annotation { "Feature Type Name" : "Feature", "Feature Type Description" : "" }
export const myFeature = defineFeature(function(context is Context, id is Id, definition is map)
    precondition{}
    {
        {
            var Q0;
            Q0=qCreatedBy(makeId("Top.planeOp"),FACE);
            var sketch = newSketch(context, id + "F0", { "sketchPlane" : qUnion([Q0])});
            skLineSegment(sketch, "E0.bottom", {"start": v(30.53, 26.5) * mm, "end": v(-34.5, 26.5) * mm});
            skLineSegment(sketch, "E0.top", {"start": v(32.26, -26.5) * mm, "end": v(-34.5, -26.5) * mm});
            skLineSegment(sketch, "E0.left", {"start": v(34.5, 10.5) * mm, "end": v(34.5, -21.5) * mm});
            skLineSegment(sketch, "E0.right", {"start": v(-34.5, 26.5) * mm, "end": v(-34.5, -26.5) * mm});
            skPoint(sketch, "E0.middle", {"position": v(0, 0) * mm});
            skPoint(sketch, "E1", {"position": v(32.26, -26.5) * mm});
            skLineSegment(sketch, "E2", {"start": v(32.26, -26.5) * mm, "end": v(32.26, -23.5) * mm});
            skLineSegment(sketch, "E3", {"start": v(32.26, -23.5) * mm, "end": v(34.5, -21.5) * mm});
            skLineSegment(sketch, "E4", {"start": v(32.26, 25.5) * mm, "end": v(32.26, 12.5) * mm});
            skLineSegment(sketch, "E5", {"start": v(32.26, 12.5) * mm, "end": v(34.5, 10.5) * mm});
            skPoint(sketch, "E6.orphan", {"position": v(34.5, 26.5) * mm});
            skPoint(sketch, "E7.orphan", {"position": v(34.5, -26.5) * mm});
            skLineSegment(sketch, "E8", {"start": v(30.53, 26.5) * mm, "end": v(32.26, 25.5) * mm});
            skPoint(sketch, "E9", {"position": v(32.26, 25.5) * mm});
            skPoint(sketch, "E10", {"position": v(32.26, 26.5) * mm});
            skLineSegment(sketch, "E11", {"start": v(32.26, 25.5) * mm, "end": v(30.53, 26.5) * mm});
            skLineSegment(sketch, "E12.bottom", {"start": v(31.26, 25.5) * mm, "end": v(11.26, 25.5) * mm});
            skLineSegment(sketch, "E12.top", {"start": v(31.26, 23.5) * mm, "end": v(11.26, 23.5) * mm});
            skLineSegment(sketch, "E12.left", {"start": v(32.26, 25.5) * mm, "end": v(32.26, 23.5) * mm});
            skLineSegment(sketch, "E12.right", {"start": v(11.26, 25.5) * mm, "end": v(11.26, 23.5) * mm});
            skLineSegment(sketch, "E13", {"start": v(31.26, 25.5) * mm, "end": v(31.26, 23.5) * mm});
            skLineSegment(sketch, "E14.bottom", {"start": v(10.26, 23.5) * mm, "end": v(-9.74, 23.5) * mm});
            skLineSegment(sketch, "E14.top", {"start": v(10.26, 25.5) * mm, "end": v(-9.74, 25.5) * mm});
            skLineSegment(sketch, "E14.left", {"start": v(11.26, 23.5) * mm, "end": v(11.26, 25.5) * mm});
            skLineSegment(sketch, "E14.right", {"start": v(-9.74, 23.5) * mm, "end": v(-9.74, 25.5) * mm});
            skLineSegment(sketch, "E15", {"start": v(10.26, 25.5) * mm, "end": v(10.26, 23.5) * mm});
            skPoint(sketch, "E16", {"position": v(32.26, -25.5) * mm});
            skLineSegment(sketch, "E17.bottom", {"start": v(31.26, -25.5) * mm, "end": v(16.26, -25.5) * mm});
            skLineSegment(sketch, "E17.top", {"start": v(31.26, -23.5) * mm, "end": v(16.26, -23.5) * mm});
            skLineSegment(sketch, "E17.left", {"start": v(32.26, -25.5) * mm, "end": v(32.26, -23.5) * mm});
            skLineSegment(sketch, "E17.right", {"start": v(0.26, -25.5) * mm, "end": v(0.26, -23.5) * mm});
            skLineSegment(sketch, "E18", {"start": v(31.26, -23.5) * mm, "end": v(31.26, -25.5) * mm});
            skLineSegment(sketch, "E19", {"start": v(16.26, -23.5) * mm, "end": v(16.26, -25.5) * mm});
            skLineSegment(sketch, "E20", {"start": v(15.26, -23.5) * mm, "end": v(15.26, -25.5) * mm});
            skLineSegment(sketch, "E21.trimOffspring", {"start": v(15.26, -23.5) * mm, "end": v(0.26, -23.5) * mm});
            skLineSegment(sketch, "E22.trimOffspring", {"start": v(15.26, -25.5) * mm, "end": v(0.26, -25.5) * mm});
            skCircle(sketch, "E23", {"center": v(32, -19) * mm, "radius": 1.5 * mm});
            skCircle(sketch, "E24", {"center": v(32, 8) * mm, "radius": 1.5 * mm});
            skCircle(sketch, "E25", {"center": v(-19, -24) * mm, "radius": 1.5 * mm});
            skCircle(sketch, "E26", {"center": v(-19, 24) * mm, "radius": 1.5 * mm});
            skLineSegment(sketch, "E27.bottom", {"start": v(-34.5, 6.5) * mm, "end": v(-33.5, 6.5) * mm});
            skLineSegment(sketch, "E27.top", {"start": v(-34.5, -4.5) * mm, "end": v(-33.5, -4.5) * mm});
            skLineSegment(sketch, "E27.left", {"start": v(-34.5, 6.5) * mm, "end": v(-34.5, -4.5) * mm});
            skLineSegment(sketch, "E27.right", {"start": v(-30.5, 6.5) * mm, "end": v(-30.5, -4.5) * mm});
            skLineSegment(sketch, "E28.top", {"start": v(-33.5, 6) * mm, "end": v(-31.5, 6) * mm});
            skLineSegment(sketch, "E28.left", {"start": v(-33.5, 6.5) * mm, "end": v(-33.5, 6) * mm});
            skLineSegment(sketch, "E28.right", {"start": v(-31.5, 6.5) * mm, "end": v(-31.5, 6) * mm});
            skLineSegment(sketch, "E29.top", {"start": v(-33.5, -4) * mm, "end": v(-31.5, -4) * mm});
            skLineSegment(sketch, "E29.left", {"start": v(-33.5, -4.5) * mm, "end": v(-33.5, -4) * mm});
            skLineSegment(sketch, "E29.right", {"start": v(-31.5, -4.5) * mm, "end": v(-31.5, -4) * mm});
            skLineSegment(sketch, "E30.trimOffspring", {"start": v(-31.5, -4.5) * mm, "end": v(-30.5, -4.5) * mm});
            skLineSegment(sketch, "E31.trimOffspring", {"start": v(-31.5, 6.5) * mm, "end": v(-30.5, 6.5) * mm});
            skLineSegment(sketch, "E32.bottom", {"start": v(-33.31, 3) * mm, "end": v(-31.69, 3) * mm});
            skLineSegment(sketch, "E32.top", {"start": v(-33.31, -1) * mm, "end": v(-31.69, -1) * mm});
            skLineSegment(sketch, "E32.left", {"start": v(-33.31, 3) * mm, "end": v(-33.31, -1) * mm});
            skLineSegment(sketch, "E32.right", {"start": v(-31.69, 3) * mm, "end": v(-31.69, -1) * mm});
            skPoint(sketch, "E32.middle", {"position": v(-32.5, 1) * mm});
            skLineSegment(sketch, "E33.bottom", {"start": v(-33.31, 0.75) * mm, "end": v(-31.69, 0.75) * mm});
            skLineSegment(sketch, "E33.left", {"start": v(-33.31, 0.75) * mm, "end": v(-33.31, -1) * mm});
            skLineSegment(sketch, "E33.right", {"start": v(-31.69, 0.75) * mm, "end": v(-31.69, -1) * mm});
            skLineSegment(sketch, "E34", {"start": v(31.26, 24.5) * mm, "end": v(-9.74, 24.5) * mm, "construction": true});
            skLineSegment(sketch, "E35", {"start": v(31.26, -24.5) * mm, "end": v(0.26, -24.5) * mm, "construction": true});
            skLineSegment(sketch, "E36.bottom", {"start": v(17.26, -25.03) * mm, "end": v(18.26, -25.03) * mm});
            skLineSegment(sketch, "E36.top", {"start": v(17.26, -24.03) * mm, "end": v(18.26, -24.03) * mm});
            skLineSegment(sketch, "E36.left", {"start": v(17.26, -25.03) * mm, "end": v(17.26, -24.03) * mm});
            skLineSegment(sketch, "E36.right", {"start": v(18.26, -25.03) * mm, "end": v(18.26, -24.03) * mm});
            skLineSegment(sketch, "E37.1.0.0", {"start": v(42.26, -24.03) * mm, "end": v(43.26, -24.03) * mm});
            skLineSegment(sketch, "E37.1.0.1", {"start": v(42.26, -25.03) * mm, "end": v(42.26, -24.03) * mm});
            skLineSegment(sketch, "E37.1.0.2", {"start": v(43.26, -25.03) * mm, "end": v(43.26, -24.03) * mm});
            skLineSegment(sketch, "E37.2.0.0", {"start": v(67.26, -24.03) * mm, "end": v(68.26, -24.03) * mm});
            skLineSegment(sketch, "E37.2.0.1", {"start": v(67.26, -25.03) * mm, "end": v(67.26, -24.03) * mm});
            skLineSegment(sketch, "E37.2.0.2", {"start": v(68.26, -25.03) * mm, "end": v(68.26, -24.03) * mm});
            skLineSegment(sketch, "E37.direction1", {"start": v(17.26, -24.03) * mm, "end": v(42.26, -24.03) * mm, "construction": true});
            skLineSegment(sketch, "E38.1.0.0", {"start": v(19.66, -24.03) * mm, "end": v(20.66, -24.03) * mm});
            skLineSegment(sketch, "E38.1.0.1", {"start": v(20.66, -25.03) * mm, "end": v(20.66, -24.03) * mm});
            skLineSegment(sketch, "E38.1.0.2", {"start": v(19.66, -25.03) * mm, "end": v(19.66, -24.03) * mm});
            skLineSegment(sketch, "E38.1.0.3", {"start": v(19.66, -25.03) * mm, "end": v(20.66, -25.03) * mm});
            skLineSegment(sketch, "E38.1.0.4", {"start": v(19.66, -24.03) * mm, "end": v(44.66, -24.03) * mm, "construction": true});
            skLineSegment(sketch, "E38.2.0.0", {"start": v(22.06, -24.03) * mm, "end": v(23.06, -24.03) * mm});
            skLineSegment(sketch, "E38.2.0.1", {"start": v(23.06, -25.03) * mm, "end": v(23.06, -24.03) * mm});
            skLineSegment(sketch, "E38.2.0.2", {"start": v(22.06, -25.03) * mm, "end": v(22.06, -24.03) * mm});
            skLineSegment(sketch, "E38.2.0.3", {"start": v(22.06, -25.03) * mm, "end": v(23.06, -25.03) * mm});
            skLineSegment(sketch, "E38.2.0.4", {"start": v(22.06, -24.03) * mm, "end": v(47.06, -24.03) * mm, "construction": true});
            skLineSegment(sketch, "E38.3.0.0", {"start": v(24.46, -24.03) * mm, "end": v(25.46, -24.03) * mm});
            skLineSegment(sketch, "E38.3.0.1", {"start": v(25.46, -25.03) * mm, "end": v(25.46, -24.03) * mm});
            skLineSegment(sketch, "E38.3.0.2", {"start": v(24.46, -25.03) * mm, "end": v(24.46, -24.03) * mm});
            skLineSegment(sketch, "E38.3.0.3", {"start": v(24.46, -25.03) * mm, "end": v(25.46, -25.03) * mm});
            skLineSegment(sketch, "E38.3.0.4", {"start": v(24.46, -24.03) * mm, "end": v(49.46, -24.03) * mm, "construction": true});
            skLineSegment(sketch, "E38.4.0.0", {"start": v(26.86, -24.03) * mm, "end": v(27.86, -24.03) * mm});
            skLineSegment(sketch, "E38.4.0.1", {"start": v(27.86, -25.03) * mm, "end": v(27.86, -24.03) * mm});
            skLineSegment(sketch, "E38.4.0.2", {"start": v(26.86, -25.03) * mm, "end": v(26.86, -24.03) * mm});
            skLineSegment(sketch, "E38.4.0.3", {"start": v(26.86, -25.03) * mm, "end": v(27.86, -25.03) * mm});
            skLineSegment(sketch, "E38.4.0.4", {"start": v(26.86, -24.03) * mm, "end": v(51.86, -24.03) * mm, "construction": true});
            skLineSegment(sketch, "E38.5.0.0", {"start": v(29.26, -24.03) * mm, "end": v(30.26, -24.03) * mm});
            skLineSegment(sketch, "E38.5.0.1", {"start": v(30.26, -25.03) * mm, "end": v(30.26, -24.03) * mm});
            skLineSegment(sketch, "E38.5.0.2", {"start": v(29.26, -25.03) * mm, "end": v(29.26, -24.03) * mm});
            skLineSegment(sketch, "E38.5.0.3", {"start": v(29.26, -25.03) * mm, "end": v(30.26, -25.03) * mm});
            skLineSegment(sketch, "E38.5.0.4", {"start": v(29.26, -24.03) * mm, "end": v(54.26, -24.03) * mm, "construction": true});
            skLineSegment(sketch, "E38.direction1", {"start": v(17.26, -24.03) * mm, "end": v(19.66, -24.03) * mm, "construction": true});
            skLineSegment(sketch, "E39.bottom", {"start": v(1.26, -25) * mm, "end": v(2.26, -25) * mm});
            skLineSegment(sketch, "E39.top", {"start": v(1.26, -24) * mm, "end": v(2.26, -24) * mm});
            skLineSegment(sketch, "E39.left", {"start": v(1.26, -25) * mm, "end": v(1.26, -24) * mm});
            skLineSegment(sketch, "E39.right", {"start": v(2.26, -25) * mm, "end": v(2.26, -24) * mm});
            skLineSegment(sketch, "E40.1.0.0", {"start": v(3.66, -24) * mm, "end": v(4.66, -24) * mm});
            skLineSegment(sketch, "E40.1.0.1", {"start": v(4.66, -25) * mm, "end": v(4.66, -24) * mm});
            skLineSegment(sketch, "E40.1.0.2", {"start": v(3.66, -25) * mm, "end": v(3.66, -24) * mm});
            skLineSegment(sketch, "E40.1.0.3", {"start": v(3.66, -25) * mm, "end": v(4.66, -25) * mm});
            skLineSegment(sketch, "E40.2.0.0", {"start": v(6.06, -24) * mm, "end": v(7.06, -24) * mm});
            skLineSegment(sketch, "E40.2.0.1", {"start": v(7.06, -25) * mm, "end": v(7.06, -24) * mm});
            skLineSegment(sketch, "E40.2.0.2", {"start": v(6.06, -25) * mm, "end": v(6.06, -24) * mm});
            skLineSegment(sketch, "E40.2.0.3", {"start": v(6.06, -25) * mm, "end": v(7.06, -25) * mm});
            skLineSegment(sketch, "E40.3.0.0", {"start": v(8.46, -24.01) * mm, "end": v(9.46, -24.01) * mm});
            skLineSegment(sketch, "E40.3.0.1", {"start": v(9.46, -25.01) * mm, "end": v(9.46, -24.01) * mm});
            skLineSegment(sketch, "E40.3.0.2", {"start": v(8.46, -25.01) * mm, "end": v(8.46, -24.01) * mm});
            skLineSegment(sketch, "E40.3.0.3", {"start": v(8.46, -25.01) * mm, "end": v(9.46, -25.01) * mm});
            skLineSegment(sketch, "E40.4.0.0", {"start": v(10.86, -24.02) * mm, "end": v(11.86, -24.02) * mm});
            skLineSegment(sketch, "E40.4.0.1", {"start": v(11.86, -25.02) * mm, "end": v(11.86, -24.02) * mm});
            skLineSegment(sketch, "E40.4.0.2", {"start": v(10.86, -25.02) * mm, "end": v(10.86, -24.02) * mm});
            skLineSegment(sketch, "E40.4.0.3", {"start": v(10.86, -25.02) * mm, "end": v(11.86, -25.02) * mm});
            skLineSegment(sketch, "E40.5.0.0", {"start": v(13.26, -24.02) * mm, "end": v(14.26, -24.02) * mm});
            skLineSegment(sketch, "E40.5.0.1", {"start": v(14.26, -25.02) * mm, "end": v(14.26, -24.02) * mm});
            skLineSegment(sketch, "E40.5.0.2", {"start": v(13.26, -25.02) * mm, "end": v(13.26, -24.02) * mm});
            skLineSegment(sketch, "E40.5.0.3", {"start": v(13.26, -25.02) * mm, "end": v(14.26, -25.02) * mm});
            skLineSegment(sketch, "E40.direction1", {"start": v(1.26, -24) * mm, "end": v(3.66, -24) * mm, "construction": true});
            skLineSegment(sketch, "E41.bottom", {"start": v(-8.74, 24.95) * mm, "end": v(-7.74, 24.95) * mm});
            skLineSegment(sketch, "E41.top", {"start": v(-8.74, 23.95) * mm, "end": v(-7.74, 23.95) * mm});
            skLineSegment(sketch, "E41.left", {"start": v(-8.74, 24.95) * mm, "end": v(-8.74, 23.95) * mm});
            skLineSegment(sketch, "E41.right", {"start": v(-7.74, 24.95) * mm, "end": v(-7.74, 23.95) * mm});
            skLineSegment(sketch, "E42.1.0.0", {"start": v(-6.3, 24.95) * mm, "end": v(-5.3, 24.95) * mm});
            skLineSegment(sketch, "E42.1.0.1", {"start": v(-5.3, 24.95) * mm, "end": v(-5.3, 23.95) * mm});
            skLineSegment(sketch, "E42.1.0.2", {"start": v(-6.3, 24.95) * mm, "end": v(-6.3, 23.95) * mm});
            skLineSegment(sketch, "E42.1.0.3", {"start": v(-6.3, 23.95) * mm, "end": v(-5.3, 23.95) * mm});
            skLineSegment(sketch, "E42.2.0.0", {"start": v(-3.88, 24.95) * mm, "end": v(-2.88, 24.95) * mm});
            skLineSegment(sketch, "E42.2.0.1", {"start": v(-2.88, 24.95) * mm, "end": v(-2.88, 23.95) * mm});
            skLineSegment(sketch, "E42.2.0.2", {"start": v(-3.88, 24.95) * mm, "end": v(-3.88, 23.95) * mm});
            skLineSegment(sketch, "E42.2.0.3", {"start": v(-3.88, 23.95) * mm, "end": v(-2.88, 23.95) * mm});
            skLineSegment(sketch, "E42.3.0.0", {"start": v(-1.45, 24.95) * mm, "end": v(-0.45, 24.95) * mm});
            skLineSegment(sketch, "E42.3.0.1", {"start": v(-0.45, 24.95) * mm, "end": v(-0.45, 23.95) * mm});
            skLineSegment(sketch, "E42.3.0.2", {"start": v(-1.45, 24.95) * mm, "end": v(-1.45, 23.95) * mm});
            skLineSegment(sketch, "E42.3.0.3", {"start": v(-1.45, 23.95) * mm, "end": v(-0.45, 23.95) * mm});
            skLineSegment(sketch, "E42.4.0.0", {"start": v(0.98, 24.95) * mm, "end": v(1.98, 24.95) * mm});
            skLineSegment(sketch, "E42.4.0.1", {"start": v(1.98, 24.95) * mm, "end": v(1.98, 23.95) * mm});
            skLineSegment(sketch, "E42.4.0.2", {"start": v(0.98, 24.95) * mm, "end": v(0.98, 23.95) * mm});
            skLineSegment(sketch, "E42.4.0.3", {"start": v(0.98, 23.95) * mm, "end": v(1.98, 23.95) * mm});
            skLineSegment(sketch, "E42.5.0.0", {"start": v(3.4, 24.95) * mm, "end": v(4.4, 24.95) * mm});
            skLineSegment(sketch, "E42.5.0.1", {"start": v(4.4, 24.95) * mm, "end": v(4.4, 23.95) * mm});
            skLineSegment(sketch, "E42.5.0.2", {"start": v(3.4, 24.95) * mm, "end": v(3.4, 23.95) * mm});
            skLineSegment(sketch, "E42.5.0.3", {"start": v(3.4, 23.95) * mm, "end": v(4.4, 23.95) * mm});
            skLineSegment(sketch, "E42.6.0.0", {"start": v(5.84, 24.95) * mm, "end": v(6.84, 24.95) * mm});
            skLineSegment(sketch, "E42.6.0.1", {"start": v(6.84, 24.95) * mm, "end": v(6.84, 23.95) * mm});
            skLineSegment(sketch, "E42.6.0.2", {"start": v(5.84, 24.95) * mm, "end": v(5.84, 23.95) * mm});
            skLineSegment(sketch, "E42.6.0.3", {"start": v(5.84, 23.95) * mm, "end": v(6.84, 23.95) * mm});
            skLineSegment(sketch, "E42.7.0.0", {"start": v(8.26, 24.95) * mm, "end": v(9.26, 24.95) * mm});
            skLineSegment(sketch, "E42.7.0.1", {"start": v(9.26, 24.95) * mm, "end": v(9.26, 23.95) * mm});
            skLineSegment(sketch, "E42.7.0.2", {"start": v(8.26, 24.95) * mm, "end": v(8.26, 23.95) * mm});
            skLineSegment(sketch, "E42.7.0.3", {"start": v(8.26, 23.95) * mm, "end": v(9.26, 23.95) * mm});
            skLineSegment(sketch, "E42.direction1", {"start": v(-8.74, 24.95) * mm, "end": v(-6.3, 24.95) * mm, "construction": true});
            skLineSegment(sketch, "E43.bottom", {"start": v(12.26, 24.97) * mm, "end": v(13.26, 24.97) * mm});
            skLineSegment(sketch, "E43.top", {"start": v(12.26, 23.97) * mm, "end": v(13.26, 23.97) * mm});
            skLineSegment(sketch, "E43.left", {"start": v(12.26, 24.97) * mm, "end": v(12.26, 23.97) * mm});
            skLineSegment(sketch, "E43.right", {"start": v(13.26, 24.97) * mm, "end": v(13.26, 23.97) * mm});
            skLineSegment(sketch, "E44.1.0.0", {"start": v(14.7, 24.97) * mm, "end": v(15.7, 24.97) * mm});
            skLineSegment(sketch, "E44.1.0.1", {"start": v(15.7, 24.97) * mm, "end": v(15.7, 23.97) * mm});
            skLineSegment(sketch, "E44.1.0.2", {"start": v(14.7, 24.97) * mm, "end": v(14.7, 23.97) * mm});
            skLineSegment(sketch, "E44.1.0.3", {"start": v(14.7, 23.97) * mm, "end": v(15.7, 23.97) * mm});
            skLineSegment(sketch, "E44.2.0.0", {"start": v(17.12, 24.97) * mm, "end": v(18.12, 24.97) * mm});
            skLineSegment(sketch, "E44.2.0.1", {"start": v(18.12, 24.97) * mm, "end": v(18.12, 23.97) * mm});
            skLineSegment(sketch, "E44.2.0.2", {"start": v(17.12, 24.97) * mm, "end": v(17.12, 23.97) * mm});
            skLineSegment(sketch, "E44.2.0.3", {"start": v(17.12, 23.97) * mm, "end": v(18.12, 23.97) * mm});
            skLineSegment(sketch, "E44.3.0.0", {"start": v(19.55, 24.97) * mm, "end": v(20.55, 24.97) * mm});
            skLineSegment(sketch, "E44.3.0.1", {"start": v(20.55, 24.97) * mm, "end": v(20.55, 23.97) * mm});
            skLineSegment(sketch, "E44.3.0.2", {"start": v(19.55, 24.97) * mm, "end": v(19.55, 23.97) * mm});
            skLineSegment(sketch, "E44.3.0.3", {"start": v(19.55, 23.97) * mm, "end": v(20.55, 23.97) * mm});
            skLineSegment(sketch, "E44.4.0.0", {"start": v(21.98, 24.97) * mm, "end": v(22.98, 24.97) * mm});
            skLineSegment(sketch, "E44.4.0.1", {"start": v(22.98, 24.97) * mm, "end": v(22.98, 23.97) * mm});
            skLineSegment(sketch, "E44.4.0.2", {"start": v(21.98, 24.97) * mm, "end": v(21.98, 23.97) * mm});
            skLineSegment(sketch, "E44.4.0.3", {"start": v(21.98, 23.97) * mm, "end": v(22.98, 23.97) * mm});
            skLineSegment(sketch, "E44.5.0.0", {"start": v(24.4, 24.97) * mm, "end": v(25.4, 24.97) * mm});
            skLineSegment(sketch, "E44.5.0.1", {"start": v(25.4, 24.97) * mm, "end": v(25.4, 23.97) * mm});
            skLineSegment(sketch, "E44.5.0.2", {"start": v(24.4, 24.97) * mm, "end": v(24.4, 23.97) * mm});
            skLineSegment(sketch, "E44.5.0.3", {"start": v(24.4, 23.97) * mm, "end": v(25.4, 23.97) * mm});
            skLineSegment(sketch, "E44.6.0.0", {"start": v(26.84, 24.97) * mm, "end": v(27.84, 24.97) * mm});
            skLineSegment(sketch, "E44.6.0.1", {"start": v(27.84, 24.97) * mm, "end": v(27.84, 23.97) * mm});
            skLineSegment(sketch, "E44.6.0.2", {"start": v(26.84, 24.97) * mm, "end": v(26.84, 23.97) * mm});
            skLineSegment(sketch, "E44.6.0.3", {"start": v(26.84, 23.97) * mm, "end": v(27.84, 23.97) * mm});
            skLineSegment(sketch, "E44.7.0.0", {"start": v(29.26, 24.97) * mm, "end": v(30.26, 24.97) * mm});
            skLineSegment(sketch, "E44.7.0.1", {"start": v(30.26, 24.97) * mm, "end": v(30.26, 23.97) * mm});
            skLineSegment(sketch, "E44.7.0.2", {"start": v(29.26, 24.97) * mm, "end": v(29.26, 23.97) * mm});
            skLineSegment(sketch, "E44.7.0.3", {"start": v(29.26, 23.97) * mm, "end": v(30.26, 23.97) * mm});
            skLineSegment(sketch, "E44.direction1", {"start": v(12.26, 24.97) * mm, "end": v(14.7, 24.97) * mm, "construction": true});
            skLineSegment(sketch, "E45.bottom", {"start": v(-0.74, -24.5) * mm, "end": v(-6.74, -24.5) * mm});
            skLineSegment(sketch, "E45.top", {"start": v(-0.74, -18.5) * mm, "end": v(-6.74, -18.5) * mm});
            skLineSegment(sketch, "E45.left", {"start": v(-0.74, -24.5) * mm, "end": v(-0.74, -18.5) * mm});
            skLineSegment(sketch, "E45.right", {"start": v(-6.74, -24.5) * mm, "end": v(-6.74, -18.5) * mm});
            skLineSegment(sketch, "E46.bottom", {"start": v(-6.74, -24.5) * mm, "end": v(-12.74, -24.5) * mm});
            skLineSegment(sketch, "E46.top", {"start": v(-6.74, -18.5) * mm, "end": v(-12.74, -18.5) * mm});
            skLineSegment(sketch, "E46.right", {"start": v(-12.74, -24.5) * mm, "end": v(-12.74, -18.5) * mm});
            skCircle(sketch, "E47", {"center": v(-3.74, -21.5) * mm, "radius": 3 * mm});
            skPoint(sketch, "E47.first.point", {"position": v(-3.74, -24.5) * mm});
            skPoint(sketch, "E47.second.point", {"position": v(-3.74, -18.5) * mm});
            skPoint(sketch, "E47.third.point", {"position": v(-5.52, -19.08) * mm});
            skCircle(sketch, "E48", {"center": v(-9.74, -21.5) * mm, "radius": 3 * mm});
            skPoint(sketch, "E48.centerSnap0", {"position": v(-9.74, -18.5) * mm});
            skPoint(sketch, "E48.centerSnap1", {"position": v(-6.74, -21.5) * mm});
            skLineSegment(sketch, "E49.bottom", {"start": v(31.26, -16.87) * mm, "end": v(0, -16.87) * mm});
            skLineSegment(sketch, "E49.top", {"start": v(31.26, -7) * mm, "end": v(0, -7) * mm});
            skLineSegment(sketch, "E49.left", {"start": v(31.26, -16.87) * mm, "end": v(31.26, -7) * mm});
            skLineSegment(sketch, "E49.right", {"start": v(0, -16.87) * mm, "end": v(0, -7) * mm});
            skLineSegment(sketch, "E50.bottom", {"start": v(20.5, 2) * mm, "end": v(24.5, 2) * mm});
            skLineSegment(sketch, "E50.top", {"start": v(20.5, -2) * mm, "end": v(24.5, -2) * mm});
            skLineSegment(sketch, "E50.left", {"start": v(20.5, 2) * mm, "end": v(20.5, -2) * mm});
            skLineSegment(sketch, "E50.right", {"start": v(24.5, 2) * mm, "end": v(24.5, -2) * mm});
            skCircle(sketch, "E51", {"center": v(22.5, 0) * mm, "radius": 1.5 * mm});
            skPoint(sketch, "E51.centerSnap0", {"position": v(24.5, 0) * mm});
            skPoint(sketch, "E51.centerSnap1", {"position": v(22.5, 2) * mm});
            skLineSegment(sketch, "E52", {"start": v(22.5, 0) * mm, "end": v(22.5, 2) * mm, "construction": true});
            skLineSegment(sketch, "E53", {"start": v(22.5, 0) * mm, "end": v(24.5, 0) * mm, "construction": true});
            skLineSegment(sketch, "E54", {"start": v(22.5, 0) * mm, "end": v(20.5, 0) * mm, "construction": true});
            skLineSegment(sketch, "E55", {"start": v(20.5, 0) * mm, "end": v(22.5, 0) * mm, "construction": true});
            skLineSegment(sketch, "E56", {"start": v(22.5, 0) * mm, "end": v(22.5, -2) * mm, "construction": true});
            skLineSegment(sketch, "E57.bottom", {"start": v(20.5, 2) * mm, "end": v(21.5, 2) * mm, "construction": true});
            skLineSegment(sketch, "E57.top", {"start": v(20.5, 1) * mm, "end": v(21.5, 1) * mm, "construction": true});
            skLineSegment(sketch, "E57.left", {"start": v(20.5, 2) * mm, "end": v(20.5, 1) * mm, "construction": true});
            skLineSegment(sketch, "E57.right", {"start": v(21.5, 2) * mm, "end": v(21.5, 1) * mm, "construction": true});
            skPoint(sketch, "E58.oppositeSnap0", {"position": v(20.5, 1.5) * mm});
            skPoint(sketch, "E58.oppositeSnap1", {"position": v(21, 2) * mm});
            skLineSegment(sketch, "E58.bottom", {"start": v(20.5, 2) * mm, "end": v(21, 2) * mm});
            skLineSegment(sketch, "E58.top", {"start": v(20.5, 1.5) * mm, "end": v(21, 1.5) * mm, "construction": true});
            skLineSegment(sketch, "E58.left", {"start": v(20.5, 2) * mm, "end": v(20.5, 1.5) * mm});
            skLineSegment(sketch, "E58.right", {"start": v(21, 2) * mm, "end": v(21, 1.5) * mm, "construction": true});
            skCircle(sketch, "E59", {"center": v(20.75, 1.75) * mm, "radius": 0.2 * mm});
            skPoint(sketch, "E59.centerSnap0", {"position": v(21, 1.75) * mm});
            skPoint(sketch, "E59.centerSnap1", {"position": v(20.75, 2) * mm});
            skPoint(sketch, "E60.firstSnap0", {"position": v(23.5, 0) * mm});
            skPoint(sketch, "E60.firstSnap1", {"position": v(22.5, 1) * mm});
            skLineSegment(sketch, "E60.bottom", {"start": v(23.5, 1) * mm, "end": v(24.5, 1) * mm, "construction": true});
            skLineSegment(sketch, "E60.top", {"start": v(23.5, 2) * mm, "end": v(24.5, 2) * mm});
            skLineSegment(sketch, "E60.left", {"start": v(23.5, 1) * mm, "end": v(23.5, 2) * mm, "construction": true});
            skLineSegment(sketch, "E60.right", {"start": v(24.5, 1) * mm, "end": v(24.5, 2) * mm});
            skPoint(sketch, "E61.firstSnap0", {"position": v(23.5, 1.5) * mm});
            skPoint(sketch, "E61.firstSnap1", {"position": v(24, 1) * mm});
            skLineSegment(sketch, "E61.bottom", {"start": v(24, 1.5) * mm, "end": v(24.5, 1.5) * mm, "construction": true});
            skLineSegment(sketch, "E61.top", {"start": v(24, 2) * mm, "end": v(24.5, 2) * mm});
            skLineSegment(sketch, "E61.left", {"start": v(24, 1.5) * mm, "end": v(24, 2) * mm, "construction": true});
            skLineSegment(sketch, "E61.right", {"start": v(24.5, 1.5) * mm, "end": v(24.5, 2) * mm});
            skCircle(sketch, "E62", {"center": v(24.25, 1.75) * mm, "radius": 0.2 * mm});
            skPoint(sketch, "E62.centerSnap0", {"position": v(24, 1.75) * mm});
            skPoint(sketch, "E62.centerSnap1", {"position": v(24.25, 1.5) * mm});
            skPoint(sketch, "E63.firstSnap0", {"position": v(22.5, -1) * mm});
            skLineSegment(sketch, "E63.bottom", {"start": v(23.5, -1) * mm, "end": v(24.5, -1) * mm, "construction": true});
            skLineSegment(sketch, "E63.top", {"start": v(23.5, -2) * mm, "end": v(24.5, -2) * mm});
            skLineSegment(sketch, "E63.left", {"start": v(23.5, -1) * mm, "end": v(23.5, -2) * mm, "construction": true});
            skLineSegment(sketch, "E63.right", {"start": v(24.5, -1) * mm, "end": v(24.5, -2) * mm});
            skLineSegment(sketch, "E64.bottom", {"start": v(24, -2) * mm, "end": v(24.5, -2) * mm});
            skLineSegment(sketch, "E64.top", {"start": v(24, -1.5) * mm, "end": v(24.5, -1.5) * mm, "construction": true});
            skLineSegment(sketch, "E64.left", {"start": v(24, -2) * mm, "end": v(24, -1.5) * mm, "construction": true});
            skLineSegment(sketch, "E64.right", {"start": v(24.5, -2) * mm, "end": v(24.5, -1.5) * mm});
            skCircle(sketch, "E65", {"center": v(24.25, -1.75) * mm, "radius": 0.2 * mm});
            skPoint(sketch, "E65.centerSnap0", {"position": v(24.5, -1.75) * mm});
            skPoint(sketch, "E65.centerSnap1", {"position": v(24.25, -2) * mm});
            skPoint(sketch, "E66.firstSnap0", {"position": v(21.5, 0) * mm});
            skLineSegment(sketch, "E66.bottom", {"start": v(21.5, -1) * mm, "end": v(20.5, -1) * mm, "construction": true});
            skLineSegment(sketch, "E66.top", {"start": v(21.5, -2) * mm, "end": v(20.5, -2) * mm});
            skLineSegment(sketch, "E66.left", {"start": v(21.5, -1) * mm, "end": v(21.5, -2) * mm, "construction": true});
            skLineSegment(sketch, "E66.right", {"start": v(20.5, -1) * mm, "end": v(20.5, -2) * mm});
            skLineSegment(sketch, "E67.bottom", {"start": v(21, -2) * mm, "end": v(20.5, -2) * mm});
            skLineSegment(sketch, "E67.top", {"start": v(21, -1.5) * mm, "end": v(20.5, -1.5) * mm, "construction": true});
            skLineSegment(sketch, "E67.left", {"start": v(21, -2) * mm, "end": v(21, -1.5) * mm, "construction": true});
            skLineSegment(sketch, "E67.right", {"start": v(20.5, -2) * mm, "end": v(20.5, -1.5) * mm});
            skCircle(sketch, "E68", {"center": v(20.75, -1.75) * mm, "radius": 0.02 * mm});
            skPoint(sketch, "E68.centerSnap0", {"position": v(21, -1.75) * mm});
            skPoint(sketch, "E68.centerSnap1", {"position": v(20.75, -1.5) * mm});
            skCircle(sketch, "E69", {"center": v(20.75, -1.75) * mm, "radius": 0.2 * mm});
            skLineSegment(sketch, "E70.bottom", {"start": v(1.2, -8.19) * mm, "end": v(30.06, -8.19) * mm});
            skLineSegment(sketch, "E70.top", {"start": v(1.2, -15.69) * mm, "end": v(30.06, -15.69) * mm});
            skLineSegment(sketch, "E70.left", {"start": v(1.2, -8.19) * mm, "end": v(1.2, -15.69) * mm});
            skLineSegment(sketch, "E70.right", {"start": v(30.06, -8.19) * mm, "end": v(30.06, -15.69) * mm});
            skPoint(sketch, "E70.middle", {"position": v(15.63, -11.94) * mm});
            skPoint(sketch, "E70.middle.positionSnap0", {"position": v(31.26, -11.94) * mm});
            skPoint(sketch, "E70.middle.positionSnap1", {"position": v(15.63, -7) * mm});
            skPoint(sketch, "E70.centerSnap0", {"position": v(31.26, -11.94) * mm});
            skPoint(sketch, "E70.centerSnap1", {"position": v(15.63, -7) * mm});
            skSolve(sketch);
        }
        {
            var Q0;
            Q0=makeQuery(id+"F0.imprint","IMPRINT",FACE,{"disambiguationData":[TD([[makeQuery(id+"F0.imprint","IMPRINT",EDGE,{"derivedFrom":sQuery(id+"F0.wireOp",EDGE,"E12.bottom")}),1.0]])]});
            var Q1;
            Q1=makeQuery(id+"F0.imprint","IMPRINT",FACE,{"disambiguationData":[TD([[makeQuery(id+"F0.imprint","IMPRINT",EDGE,{"derivedFrom":sQuery(id+"F0.wireOp",EDGE,"E14.bottom")}),-1.0]])]});
            var Q2;
            Q2=makeQuery(id+"F0.imprint","IMPRINT",FACE,{"disambiguationData":[TD([[makeQuery(id+"F0.imprint","IMPRINT",EDGE,{"derivedFrom":sQuery(id+"F0.wireOp",EDGE,"E17.bottom")}),-1.0]])]});
            var Q3;
            Q3=makeQuery(id+"F0.imprint","IMPRINT",FACE,{"disambiguationData":[TD([[makeQuery(id+"F0.imprint","IMPRINT",EDGE,{"derivedFrom":sQuery(id+"F0.wireOp",EDGE,"E17.right")}),-1.0]])]});
            extrude(context, id + "F1", {"entities" : qUnion([Q0, Q1, Q2, Q3]), "depth" : 8 * mm});
        }
        {
            var Q0;
            {var subQ1=sQuery(id+"F0.wireOp",EDGE,"E0.bottom");Q0=makeQuery(id+"F0.imprint","IMPRINT",FACE,{"disambiguationData":[TD([[makeQuery(id+"F0.imprint","IMPRINT",EDGE,{"derivedFrom":subQ1}),1.0]])]});}
            var Q1;
            Q1=makeQuery(id+"F0.imprint","IMPRINT",FACE,{"disambiguationData":[TD([[makeQuery(id+"F0.imprint","IMPRINT",EDGE,{"derivedFrom":sQuery(id+"F0.wireOp",EDGE,"E27.bottom")}),-1.0]])]});
            var Q2;
            Q2=makeQuery(id+"F0.imprint","IMPRINT",FACE,{"disambiguationData":[TD([[makeQuery(id+"F0.imprint","IMPRINT",EDGE,{"derivedFrom":sQuery(id+"F0.wireOp",EDGE,"E33.bottom")}),-1.0]])]});
            var Q3;
            Q3=makeQuery(id+"F0.imprint","IMPRINT",FACE,{"disambiguationData":[TD([[makeQuery(id+"F0.imprint","IMPRINT",EDGE,{"derivedFrom":sQuery(id+"F0.wireOp",EDGE,"E17.right")}),-1.0]])]});
            var Q4;
            Q4=makeQuery(id+"F0.imprint","IMPRINT",FACE,{"disambiguationData":[TD([[makeQuery(id+"F0.imprint","IMPRINT",EDGE,{"derivedFrom":sQuery(id+"F0.wireOp",EDGE,"E14.bottom")}),-1.0]])]});
            var Q5;
            Q5=makeQuery(id+"F0.imprint","IMPRINT",FACE,{"disambiguationData":[TD([[makeQuery(id+"F0.imprint","IMPRINT",EDGE,{"derivedFrom":sQuery(id+"F0.wireOp",EDGE,"E32.bottom")}),-1.0]])]});
            var Q6;
            Q6=makeQuery(id+"F0.imprint","IMPRINT",FACE,{"disambiguationData":[TD([[makeQuery(id+"F0.imprint","IMPRINT",EDGE,{"derivedFrom":sQuery(id+"F0.wireOp",EDGE,"E40.3.0.0")}),-1.0]])]});
            var Q7;
            Q7=makeQuery(id+"F0.imprint","IMPRINT",FACE,{"disambiguationData":[TD([[makeQuery(id+"F0.imprint","IMPRINT",EDGE,{"derivedFrom":sQuery(id+"F0.wireOp",EDGE,"E40.4.0.0")}),-1.0]])]});
            var Q8;
            Q8=makeQuery(id+"F0.imprint","IMPRINT",FACE,{"disambiguationData":[TD([[makeQuery(id+"F0.imprint","IMPRINT",EDGE,{"derivedFrom":sQuery(id+"F0.wireOp",EDGE,"E40.5.0.0")}),-1.0]])]});
            var Q9;
            Q9=makeQuery(id+"F0.imprint","IMPRINT",FACE,{"disambiguationData":[TD([[makeQuery(id+"F0.imprint","IMPRINT",EDGE,{"derivedFrom":sQuery(id+"F0.wireOp",EDGE,"E36.bottom")}),1.0]])]});
            var Q10;
            Q10=makeQuery(id+"F0.imprint","IMPRINT",FACE,{"disambiguationData":[TD([[makeQuery(id+"F0.imprint","IMPRINT",EDGE,{"derivedFrom":sQuery(id+"F0.wireOp",EDGE,"E38.1.0.0")}),-1.0]])]});
            var Q11;
            Q11=makeQuery(id+"F0.imprint","IMPRINT",FACE,{"disambiguationData":[TD([[makeQuery(id+"F0.imprint","IMPRINT",EDGE,{"derivedFrom":sQuery(id+"F0.wireOp",EDGE,"E38.2.0.0")}),-1.0]])]});
            var Q12;
            Q12=makeQuery(id+"F0.imprint","IMPRINT",FACE,{"disambiguationData":[TD([[makeQuery(id+"F0.imprint","IMPRINT",EDGE,{"derivedFrom":sQuery(id+"F0.wireOp",EDGE,"E38.4.0.0")}),-1.0]])]});
            var Q13;
            Q13=makeQuery(id+"F0.imprint","IMPRINT",FACE,{"disambiguationData":[TD([[makeQuery(id+"F0.imprint","IMPRINT",EDGE,{"derivedFrom":sQuery(id+"F0.wireOp",EDGE,"E38.5.0.0")}),-1.0]])]});
            var Q14;
            Q14=makeQuery(id+"F0.imprint","IMPRINT",FACE,{"disambiguationData":[TD([[makeQuery(id+"F0.imprint","IMPRINT",EDGE,{"derivedFrom":sQuery(id+"F0.wireOp",EDGE,"E38.3.0.0")}),-1.0]])]});
            var Q15;
            Q15=makeQuery(id+"F0.imprint","IMPRINT",FACE,{"disambiguationData":[TD([[makeQuery(id+"F0.imprint","IMPRINT",EDGE,{"derivedFrom":sQuery(id+"F0.wireOp",EDGE,"E17.bottom")}),-1.0]])]});
            var Q16;
            Q16=makeQuery(id+"F0.imprint","IMPRINT",FACE,{"disambiguationData":[TD([[makeQuery(id+"F0.imprint","IMPRINT",EDGE,{"derivedFrom":sQuery(id+"F0.wireOp",EDGE,"E41.bottom")}),-1.0]])]});
            var Q17;
            Q17=makeQuery(id+"F0.imprint","IMPRINT",FACE,{"disambiguationData":[TD([[makeQuery(id+"F0.imprint","IMPRINT",EDGE,{"derivedFrom":sQuery(id+"F0.wireOp",EDGE,"E42.1.0.0")}),-1.0]])]});
            var Q18;
            Q18=makeQuery(id+"F0.imprint","IMPRINT",FACE,{"disambiguationData":[TD([[makeQuery(id+"F0.imprint","IMPRINT",EDGE,{"derivedFrom":sQuery(id+"F0.wireOp",EDGE,"E42.2.0.0")}),-1.0]])]});
            var Q19;
            Q19=makeQuery(id+"F0.imprint","IMPRINT",FACE,{"disambiguationData":[TD([[makeQuery(id+"F0.imprint","IMPRINT",EDGE,{"derivedFrom":sQuery(id+"F0.wireOp",EDGE,"E42.3.0.0")}),-1.0]])]});
            var Q20;
            Q20=makeQuery(id+"F0.imprint","IMPRINT",FACE,{"disambiguationData":[TD([[makeQuery(id+"F0.imprint","IMPRINT",EDGE,{"derivedFrom":sQuery(id+"F0.wireOp",EDGE,"E42.4.0.0")}),-1.0]])]});
            var Q21;
            Q21=makeQuery(id+"F0.imprint","IMPRINT",FACE,{"disambiguationData":[TD([[makeQuery(id+"F0.imprint","IMPRINT",EDGE,{"derivedFrom":sQuery(id+"F0.wireOp",EDGE,"E42.5.0.0")}),-1.0]])]});
            var Q22;
            Q22=makeQuery(id+"F0.imprint","IMPRINT",FACE,{"disambiguationData":[TD([[makeQuery(id+"F0.imprint","IMPRINT",EDGE,{"derivedFrom":sQuery(id+"F0.wireOp",EDGE,"E42.6.0.0")}),-1.0]])]});
            var Q23;
            Q23=makeQuery(id+"F0.imprint","IMPRINT",FACE,{"disambiguationData":[TD([[makeQuery(id+"F0.imprint","IMPRINT",EDGE,{"derivedFrom":sQuery(id+"F0.wireOp",EDGE,"E42.7.0.0")}),-1.0]])]});
            var Q24;
            Q24=makeQuery(id+"F0.imprint","IMPRINT",FACE,{"disambiguationData":[TD([[makeQuery(id+"F0.imprint","IMPRINT",EDGE,{"derivedFrom":sQuery(id+"F0.wireOp",EDGE,"E43.bottom")}),-1.0]])]});
            var Q25;
            Q25=makeQuery(id+"F0.imprint","IMPRINT",FACE,{"disambiguationData":[TD([[makeQuery(id+"F0.imprint","IMPRINT",EDGE,{"derivedFrom":sQuery(id+"F0.wireOp",EDGE,"E44.2.0.0")}),-1.0]])]});
            var Q26;
            Q26=makeQuery(id+"F0.imprint","IMPRINT",FACE,{"disambiguationData":[TD([[makeQuery(id+"F0.imprint","IMPRINT",EDGE,{"derivedFrom":sQuery(id+"F0.wireOp",EDGE,"E44.3.0.0")}),-1.0]])]});
            var Q27;
            Q27=makeQuery(id+"F0.imprint","IMPRINT",FACE,{"disambiguationData":[TD([[makeQuery(id+"F0.imprint","IMPRINT",EDGE,{"derivedFrom":sQuery(id+"F0.wireOp",EDGE,"E44.4.0.0")}),-1.0]])]});
            var Q28;
            Q28=makeQuery(id+"F0.imprint","IMPRINT",FACE,{"disambiguationData":[TD([[makeQuery(id+"F0.imprint","IMPRINT",EDGE,{"derivedFrom":sQuery(id+"F0.wireOp",EDGE,"E44.5.0.0")}),-1.0]])]});
            var Q29;
            Q29=makeQuery(id+"F0.imprint","IMPRINT",FACE,{"disambiguationData":[TD([[makeQuery(id+"F0.imprint","IMPRINT",EDGE,{"derivedFrom":sQuery(id+"F0.wireOp",EDGE,"E44.6.0.0")}),-1.0]])]});
            var Q30;
            Q30=makeQuery(id+"F0.imprint","IMPRINT",FACE,{"disambiguationData":[TD([[makeQuery(id+"F0.imprint","IMPRINT",EDGE,{"derivedFrom":sQuery(id+"F0.wireOp",EDGE,"E44.7.0.0")}),-1.0]])]});
            var Q31;
            Q31=makeQuery(id+"F0.imprint","IMPRINT",FACE,{"disambiguationData":[TD([[makeQuery(id+"F0.imprint","IMPRINT",EDGE,{"derivedFrom":sQuery(id+"F0.wireOp",EDGE,"E12.bottom")}),1.0]])]});
            var Q32;
            Q32=makeQuery(id+"F0.imprint","IMPRINT",FACE,{"disambiguationData":[TD([[makeQuery(id+"F0.imprint","IMPRINT",EDGE,{"derivedFrom":sQuery(id+"F0.wireOp",EDGE,"E44.1.0.0")}),-1.0]])]});
            var Q33;
            Q33=makeQuery(id+"F0.imprint","IMPRINT",FACE,{"disambiguationData":[TD([[makeQuery(id+"F0.imprint","IMPRINT",EDGE,{"derivedFrom":sQuery(id+"F0.wireOp",EDGE,"E39.bottom")}),1.0]])]});
            var Q34;
            Q34=makeQuery(id+"F0.imprint","IMPRINT",FACE,{"disambiguationData":[TD([[makeQuery(id+"F0.imprint","IMPRINT",EDGE,{"derivedFrom":sQuery(id+"F0.wireOp",EDGE,"E40.1.0.0")}),-1.0]])]});
            var Q35;
            Q35=makeQuery(id+"F0.imprint","IMPRINT",FACE,{"disambiguationData":[TD([[makeQuery(id+"F0.imprint","IMPRINT",EDGE,{"derivedFrom":sQuery(id+"F0.wireOp",EDGE,"E40.2.0.0")}),-1.0]])]});
            var Q36;
            {var subQ1=sQuery(id+"F0.wireOp",EDGE,"E45.top");var subQ3=sQuery(id+"F0.wireOp",EDGE,"E47");var subQ4=makeQuery(id+"F0.imprint","INTERSECT",VERTEX,{"derivedFrom":[subQ1,subQ3]});Q36=makeQuery(id+"F0.imprint","IMPRINT",FACE,{"disambiguationData":[TD([[makeQuery(id+"F0.imprint","IMPRINT",EDGE,{"disambiguationData":[TD([[subQ4,-1.0]])],"derivedFrom":subQ1}),1.0]])]});}
            var Q37;
            {var subQ0=sQuery(id+"F0.wireOp",EDGE,"E45.left");var subQ1=sQuery(id+"F0.wireOp",EDGE,"E45.top");var subQ2=makeQuery(id+"F0.imprint","INTERSECT",VERTEX,{"derivedFrom":[subQ1,subQ0]});Q37=makeQuery(id+"F0.imprint","IMPRINT",FACE,{"disambiguationData":[TD([[makeQuery(id+"F0.imprint","IMPRINT",EDGE,{"disambiguationData":[TD([[subQ2,-1.0]])],"derivedFrom":subQ1}),1.0]])]});}
            var Q38;
            {var subQ0=sQuery(id+"F0.wireOp",EDGE,"E47");var subQ1=makeQuery(id+"F0.imprint","INTERSECT",VERTEX,{"derivedFrom":[sQuery(id+"F0.wireOp",EDGE,"E45.top"),subQ0]});Q38=makeQuery(id+"F0.imprint","IMPRINT",FACE,{"disambiguationData":[TD([[makeQuery(id+"F0.imprint","IMPRINT",EDGE,{"disambiguationData":[TD([[subQ1,1.0]])],"derivedFrom":subQ0}),1.0]])]});}
            var Q39;
            {var subQ1=sQuery(id+"F0.wireOp",EDGE,"E45.bottom");var subQ3=sQuery(id+"F0.wireOp",EDGE,"E47");var subQ4=makeQuery(id+"F0.imprint","INTERSECT",VERTEX,{"derivedFrom":[subQ1,subQ3]});Q39=makeQuery(id+"F0.imprint","IMPRINT",FACE,{"disambiguationData":[TD([[makeQuery(id+"F0.imprint","IMPRINT",EDGE,{"disambiguationData":[TD([[subQ4,-1.0]])],"derivedFrom":subQ1}),-1.0]])]});}
            var Q40;
            {var subQ0=sQuery(id+"F0.wireOp",EDGE,"E45.left");var subQ1=sQuery(id+"F0.wireOp",EDGE,"E45.bottom");var subQ2=makeQuery(id+"F0.imprint","INTERSECT",VERTEX,{"derivedFrom":[subQ1,subQ0]});Q40=makeQuery(id+"F0.imprint","IMPRINT",FACE,{"disambiguationData":[TD([[makeQuery(id+"F0.imprint","IMPRINT",EDGE,{"disambiguationData":[TD([[subQ2,-1.0]])],"derivedFrom":subQ1}),-1.0]])]});}
            var Q41;
            {var subQ1=sQuery(id+"F0.wireOp",EDGE,"E46.bottom");var subQ3=sQuery(id+"F0.wireOp",EDGE,"E48");var subQ4=makeQuery(id+"F0.imprint","INTERSECT",VERTEX,{"derivedFrom":[subQ1,subQ3]});Q41=makeQuery(id+"F0.imprint","IMPRINT",FACE,{"disambiguationData":[TD([[makeQuery(id+"F0.imprint","IMPRINT",EDGE,{"disambiguationData":[TD([[subQ4,1.0]])],"derivedFrom":subQ1}),-1.0]])]});}
            var Q42;
            {var subQ0=sQuery(id+"F0.wireOp",EDGE,"E48");var subQ1=makeQuery(id+"F0.imprint","INTERSECT",VERTEX,{"derivedFrom":[sQuery(id+"F0.wireOp",EDGE,"E46.top"),subQ0]});Q42=makeQuery(id+"F0.imprint","IMPRINT",FACE,{"disambiguationData":[TD([[makeQuery(id+"F0.imprint","IMPRINT",EDGE,{"disambiguationData":[TD([[subQ1,-1.0]])],"derivedFrom":subQ0}),1.0]])]});}
            var Q43;
            {var subQ0=sQuery(id+"F0.wireOp",EDGE,"E46.right");var subQ1=sQuery(id+"F0.wireOp",EDGE,"E46.bottom");var subQ2=makeQuery(id+"F0.imprint","INTERSECT",VERTEX,{"derivedFrom":[subQ1,subQ0]});Q43=makeQuery(id+"F0.imprint","IMPRINT",FACE,{"disambiguationData":[TD([[makeQuery(id+"F0.imprint","IMPRINT",EDGE,{"disambiguationData":[TD([[subQ2,1.0]])],"derivedFrom":subQ1}),-1.0]])]});}
            var Q44;
            {var subQ0=sQuery(id+"F0.wireOp",EDGE,"E46.right");var subQ1=sQuery(id+"F0.wireOp",EDGE,"E46.top");var subQ2=makeQuery(id+"F0.imprint","INTERSECT",VERTEX,{"derivedFrom":[subQ1,subQ0]});Q44=makeQuery(id+"F0.imprint","IMPRINT",FACE,{"disambiguationData":[TD([[makeQuery(id+"F0.imprint","IMPRINT",EDGE,{"disambiguationData":[TD([[subQ2,1.0]])],"derivedFrom":subQ1}),1.0]])]});}
            var Q45;
            {var subQ1=sQuery(id+"F0.wireOp",EDGE,"E46.top");var subQ3=sQuery(id+"F0.wireOp",EDGE,"E48");var subQ4=makeQuery(id+"F0.imprint","INTERSECT",VERTEX,{"derivedFrom":[subQ1,subQ3]});Q45=makeQuery(id+"F0.imprint","IMPRINT",FACE,{"disambiguationData":[TD([[makeQuery(id+"F0.imprint","IMPRINT",EDGE,{"disambiguationData":[TD([[subQ4,1.0]])],"derivedFrom":subQ1}),1.0]])]});}
            var Q46;
            Q46=makeQuery(id+"F0.imprint","IMPRINT",FACE,{"disambiguationData":[TD([[makeQuery(id+"F0.imprint","IMPRINT",EDGE,{"derivedFrom":sQuery(id+"F0.wireOp",EDGE,"E49.bottom")}),-1.0]])]});
            var Q47;
            Q47=makeQuery(id+"F0.imprint","IMPRINT",FACE,{"disambiguationData":[TD([[makeQuery(id+"F0.imprint","IMPRINT",EDGE,{"derivedFrom":sQuery(id+"F0.wireOp",EDGE,"E51")}),1.0]])]});
            var Q48;
            Q48=makeQuery(id+"F0.imprint","IMPRINT",FACE,{"disambiguationData":[TD([[makeQuery(id+"F0.imprint","IMPRINT",EDGE,{"derivedFrom":sQuery(id+"F0.wireOp",EDGE,"E50.bottom")}),-1.0]])]});
            var Q49;
            Q49=makeQuery(id+"F0.imprint","IMPRINT",FACE,{"disambiguationData":[TD([[makeQuery(id+"F0.imprint","IMPRINT",EDGE,{"derivedFrom":sQuery(id+"F0.wireOp",EDGE,"E68")}),-1.0]])]});
            var Q50;
            Q50=makeQuery(id+"F0.imprint","IMPRINT",FACE,{"disambiguationData":[TD([[makeQuery(id+"F0.imprint","IMPRINT",EDGE,{"derivedFrom":sQuery(id+"F0.wireOp",EDGE,"E65")}),1.0]])]});
            var Q51;
            Q51=makeQuery(id+"F0.imprint","IMPRINT",FACE,{"disambiguationData":[TD([[makeQuery(id+"F0.imprint","IMPRINT",EDGE,{"derivedFrom":sQuery(id+"F0.wireOp",EDGE,"E62")}),1.0]])]});
            var Q52;
            Q52=makeQuery(id+"F0.imprint","IMPRINT",FACE,{"disambiguationData":[TD([[makeQuery(id+"F0.imprint","IMPRINT",EDGE,{"derivedFrom":sQuery(id+"F0.wireOp",EDGE,"E59")}),1.0]])]});
            var Q53;
            Q53=makeQuery(id+"F0.imprint","IMPRINT",FACE,{"disambiguationData":[TD([[makeQuery(id+"F0.imprint","IMPRINT",EDGE,{"derivedFrom":sQuery(id+"F0.wireOp",EDGE,"E70.bottom")}),-1.0]])]});
            extrude(context, id + "F2", {"entities" : qUnion([Q0, Q1, Q2, Q3, Q4, Q5, Q6, Q7, Q8, Q9, Q10, Q11, Q12, Q13, Q14, Q15, Q16, Q17, Q18, Q19, Q20, Q21, Q22, Q23, Q24, Q25, Q26, Q27, Q28, Q29, Q30, Q31, Q32, Q33, Q34, Q35, Q36, Q37, Q38, Q39, Q40, Q41, Q42, Q43, Q44, Q45, Q46, Q47, Q48, Q49, Q50, Q51, Q52, Q53]), "oppositeDirection" : true, "depth" : 1 * mm});
        }
        {
            var Q0;
            Q0=makeQuery(id+"F0.imprint","IMPRINT",FACE,{"disambiguationData":[TD([[makeQuery(id+"F0.imprint","IMPRINT",EDGE,{"derivedFrom":sQuery(id+"F0.wireOp",EDGE,"E27.bottom")}),-1.0]])]});
            extrude(context, id + "F3", {"entities" : qUnion([Q0]), "depth" : 5 * mm});
        }
        {
            var Q0;
            Q0=makeQuery(id+"F0.imprint","IMPRINT",FACE,{"disambiguationData":[TD([[makeQuery(id+"F0.imprint","IMPRINT",EDGE,{"derivedFrom":sQuery(id+"F0.wireOp",EDGE,"E32.bottom")}),-1.0]])]});
            var Q1;
            Q1=makeQuery(id+"F0.imprint","IMPRINT",FACE,{"disambiguationData":[TD([[makeQuery(id+"F0.imprint","IMPRINT",EDGE,{"derivedFrom":sQuery(id+"F0.wireOp",EDGE,"E33.bottom")}),-1.0]])]});
            extrude(context, id + "F4", {"entities" : qUnion([Q0, Q1]), "depth" : 3.5 * mm});
        }
        {
            var Q0;
            Q0=makeQuery(id+"F0.imprint","IMPRINT",FACE,{"disambiguationData":[TD([[makeQuery(id+"F0.imprint","IMPRINT",EDGE,{"derivedFrom":sQuery(id+"F0.wireOp",EDGE,"E33.bottom")}),-1.0]])]});
            extrude(context, id + "F5", {"entities" : qUnion([Q0]), "depth" : 6.5 * mm});
        }
        {
            var Q0;
            Q0=makeQuery(id+"F2.opExtrude","CAP_FACE",FACE,{"disambiguationData":[OSD([sQuery(id+"F0.wireOp",EDGE,"E0.bottom"),sQuery(id+"F0.wireOp",EDGE,"E0.top"),sQuery(id+"F0.wireOp",EDGE,"E0.left"),sQuery(id+"F0.wireOp",EDGE,"E0.right"),sQuery(id+"F0.wireOp",EDGE,"E2"),sQuery(id+"F0.wireOp",EDGE,"E3"),sQuery(id+"F0.wireOp",EDGE,"E4"),sQuery(id+"F0.wireOp",EDGE,"E5"),sQuery(id+"F0.wireOp",EDGE,"E11"),sQuery(id+"F0.wireOp",EDGE,"E12.left"),sQuery(id+"F0.wireOp",EDGE,"E17.left"),sQuery(id+"F0.wireOp",EDGE,"E23"),sQuery(id+"F0.wireOp",EDGE,"E24"),sQuery(id+"F0.wireOp",EDGE,"E25"),sQuery(id+"F0.wireOp",EDGE,"E26"),sQuery(id+"F0.wireOp",EDGE,"E27.left"),sQuery(id+"F0.wireOp",EDGE,"E36.bottom"),sQuery(id+"F0.wireOp",EDGE,"E36.top"),sQuery(id+"F0.wireOp",EDGE,"E36.left"),sQuery(id+"F0.wireOp",EDGE,"E36.right"),sQuery(id+"F0.wireOp",EDGE,"E38.1.0.0"),sQuery(id+"F0.wireOp",EDGE,"E38.1.0.1"),sQuery(id+"F0.wireOp",EDGE,"E38.1.0.2"),sQuery(id+"F0.wireOp",EDGE,"E38.1.0.3"),sQuery(id+"F0.wireOp",EDGE,"E38.2.0.0"),sQuery(id+"F0.wireOp",EDGE,"E38.2.0.1"),sQuery(id+"F0.wireOp",EDGE,"E38.2.0.2"),sQuery(id+"F0.wireOp",EDGE,"E38.2.0.3"),sQuery(id+"F0.wireOp",EDGE,"E38.3.0.0"),sQuery(id+"F0.wireOp",EDGE,"E38.3.0.1"),sQuery(id+"F0.wireOp",EDGE,"E38.3.0.2"),sQuery(id+"F0.wireOp",EDGE,"E38.3.0.3"),sQuery(id+"F0.wireOp",EDGE,"E38.4.0.0"),sQuery(id+"F0.wireOp",EDGE,"E38.4.0.1"),sQuery(id+"F0.wireOp",EDGE,"E38.4.0.2"),sQuery(id+"F0.wireOp",EDGE,"E38.4.0.3"),sQuery(id+"F0.wireOp",EDGE,"E38.5.0.0"),sQuery(id+"F0.wireOp",EDGE,"E38.5.0.1"),sQuery(id+"F0.wireOp",EDGE,"E38.5.0.2"),sQuery(id+"F0.wireOp",EDGE,"E38.5.0.3"),sQuery(id+"F0.wireOp",EDGE,"E39.bottom"),sQuery(id+"F0.wireOp",EDGE,"E39.top"),sQuery(id+"F0.wireOp",EDGE,"E39.left"),sQuery(id+"F0.wireOp",EDGE,"E39.right"),sQuery(id+"F0.wireOp",EDGE,"E40.1.0.0"),sQuery(id+"F0.wireOp",EDGE,"E40.1.0.1"),sQuery(id+"F0.wireOp",EDGE,"E40.1.0.2"),sQuery(id+"F0.wireOp",EDGE,"E40.1.0.3"),sQuery(id+"F0.wireOp",EDGE,"E40.2.0.0"),sQuery(id+"F0.wireOp",EDGE,"E40.2.0.1"),sQuery(id+"F0.wireOp",EDGE,"E40.2.0.2"),sQuery(id+"F0.wireOp",EDGE,"E40.2.0.3"),sQuery(id+"F0.wireOp",EDGE,"E40.3.0.0"),sQuery(id+"F0.wireOp",EDGE,"E40.3.0.1"),sQuery(id+"F0.wireOp",EDGE,"E40.3.0.2"),sQuery(id+"F0.wireOp",EDGE,"E40.3.0.3"),sQuery(id+"F0.wireOp",EDGE,"E40.4.0.0"),sQuery(id+"F0.wireOp",EDGE,"E40.4.0.1"),sQuery(id+"F0.wireOp",EDGE,"E40.4.0.2"),sQuery(id+"F0.wireOp",EDGE,"E40.4.0.3"),sQuery(id+"F0.wireOp",EDGE,"E40.5.0.0"),sQuery(id+"F0.wireOp",EDGE,"E40.5.0.1"),sQuery(id+"F0.wireOp",EDGE,"E40.5.0.2"),sQuery(id+"F0.wireOp",EDGE,"E40.5.0.3")])],"isStart":false});
            var sketch = newSketch(context, id + "F6", { "sketchPlane" : qUnion([Q0])});
            skText(sketch, "E71", { "text": "Michael Ma\nDerek Ni", "fontName": "OpenSans-Regular.ttf"});
            const initialGuessF6  = {"E71": [-0.03158, 0.0108, 1, 0, 0.00415]};
            skSetInitialGuess(sketch, initialGuessF6);
            skSolve(sketch);
        }
        {
            var Q0;
            Q0 = qSketchRegion(id + "F6", true);
            extrude(context, id + "F7", {"entities" : qUnion([Q0]), "operationType" : NewBodyOperationType.REMOVE, "oppositeDirection" : true, "depth" : .1 * mm});
        }
        {
            var Q0;
            {var subQ1=sQuery(id+"F0.wireOp",EDGE,"E46.top");var subQ3=sQuery(id+"F0.wireOp",EDGE,"E48");var subQ4=makeQuery(id+"F0.imprint","INTERSECT",VERTEX,{"derivedFrom":[subQ1,subQ3]});Q0=makeQuery(id+"F0.imprint","IMPRINT",FACE,{"disambiguationData":[TD([[makeQuery(id+"F0.imprint","IMPRINT",EDGE,{"disambiguationData":[TD([[subQ4,1.0]])],"derivedFrom":subQ1}),1.0]])]});}
            var Q1;
            {var subQ0=sQuery(id+"F0.wireOp",EDGE,"E46.right");var subQ1=sQuery(id+"F0.wireOp",EDGE,"E46.top");var subQ2=makeQuery(id+"F0.imprint","INTERSECT",VERTEX,{"derivedFrom":[subQ1,subQ0]});Q1=makeQuery(id+"F0.imprint","IMPRINT",FACE,{"disambiguationData":[TD([[makeQuery(id+"F0.imprint","IMPRINT",EDGE,{"disambiguationData":[TD([[subQ2,1.0]])],"derivedFrom":subQ1}),1.0]])]});}
            var Q2;
            {var subQ0=sQuery(id+"F0.wireOp",EDGE,"E46.right");var subQ1=sQuery(id+"F0.wireOp",EDGE,"E46.bottom");var subQ2=makeQuery(id+"F0.imprint","INTERSECT",VERTEX,{"derivedFrom":[subQ1,subQ0]});Q2=makeQuery(id+"F0.imprint","IMPRINT",FACE,{"disambiguationData":[TD([[makeQuery(id+"F0.imprint","IMPRINT",EDGE,{"disambiguationData":[TD([[subQ2,1.0]])],"derivedFrom":subQ1}),-1.0]])]});}
            var Q3;
            {var subQ1=sQuery(id+"F0.wireOp",EDGE,"E46.bottom");var subQ3=sQuery(id+"F0.wireOp",EDGE,"E48");var subQ4=makeQuery(id+"F0.imprint","INTERSECT",VERTEX,{"derivedFrom":[subQ1,subQ3]});Q3=makeQuery(id+"F0.imprint","IMPRINT",FACE,{"disambiguationData":[TD([[makeQuery(id+"F0.imprint","IMPRINT",EDGE,{"disambiguationData":[TD([[subQ4,1.0]])],"derivedFrom":subQ1}),-1.0]])]});}
            var Q4;
            {var subQ0=sQuery(id+"F0.wireOp",EDGE,"E48");var subQ1=makeQuery(id+"F0.imprint","INTERSECT",VERTEX,{"derivedFrom":[sQuery(id+"F0.wireOp",EDGE,"E46.top"),subQ0]});Q4=makeQuery(id+"F0.imprint","IMPRINT",FACE,{"disambiguationData":[TD([[makeQuery(id+"F0.imprint","IMPRINT",EDGE,{"disambiguationData":[TD([[subQ1,-1.0]])],"derivedFrom":subQ0}),1.0]])]});}
            var Q5;
            {var subQ0=sQuery(id+"F0.wireOp",EDGE,"E47");var subQ1=makeQuery(id+"F0.imprint","INTERSECT",VERTEX,{"derivedFrom":[sQuery(id+"F0.wireOp",EDGE,"E45.top"),subQ0]});Q5=makeQuery(id+"F0.imprint","IMPRINT",FACE,{"disambiguationData":[TD([[makeQuery(id+"F0.imprint","IMPRINT",EDGE,{"disambiguationData":[TD([[subQ1,1.0]])],"derivedFrom":subQ0}),1.0]])]});}
            var Q6;
            {var subQ1=sQuery(id+"F0.wireOp",EDGE,"E45.top");var subQ3=sQuery(id+"F0.wireOp",EDGE,"E47");var subQ4=makeQuery(id+"F0.imprint","INTERSECT",VERTEX,{"derivedFrom":[subQ1,subQ3]});Q6=makeQuery(id+"F0.imprint","IMPRINT",FACE,{"disambiguationData":[TD([[makeQuery(id+"F0.imprint","IMPRINT",EDGE,{"disambiguationData":[TD([[subQ4,-1.0]])],"derivedFrom":subQ1}),1.0]])]});}
            var Q7;
            {var subQ0=sQuery(id+"F0.wireOp",EDGE,"E45.left");var subQ1=sQuery(id+"F0.wireOp",EDGE,"E45.top");var subQ2=makeQuery(id+"F0.imprint","INTERSECT",VERTEX,{"derivedFrom":[subQ1,subQ0]});Q7=makeQuery(id+"F0.imprint","IMPRINT",FACE,{"disambiguationData":[TD([[makeQuery(id+"F0.imprint","IMPRINT",EDGE,{"disambiguationData":[TD([[subQ2,-1.0]])],"derivedFrom":subQ1}),1.0]])]});}
            var Q8;
            {var subQ0=sQuery(id+"F0.wireOp",EDGE,"E45.left");var subQ1=sQuery(id+"F0.wireOp",EDGE,"E45.bottom");var subQ2=makeQuery(id+"F0.imprint","INTERSECT",VERTEX,{"derivedFrom":[subQ1,subQ0]});Q8=makeQuery(id+"F0.imprint","IMPRINT",FACE,{"disambiguationData":[TD([[makeQuery(id+"F0.imprint","IMPRINT",EDGE,{"disambiguationData":[TD([[subQ2,-1.0]])],"derivedFrom":subQ1}),-1.0]])]});}
            var Q9;
            {var subQ1=sQuery(id+"F0.wireOp",EDGE,"E45.bottom");var subQ3=sQuery(id+"F0.wireOp",EDGE,"E47");var subQ4=makeQuery(id+"F0.imprint","INTERSECT",VERTEX,{"derivedFrom":[subQ1,subQ3]});Q9=makeQuery(id+"F0.imprint","IMPRINT",FACE,{"disambiguationData":[TD([[makeQuery(id+"F0.imprint","IMPRINT",EDGE,{"disambiguationData":[TD([[subQ4,-1.0]])],"derivedFrom":subQ1}),-1.0]])]});}
            extrude(context, id + "F8", {"entities" : qUnion([Q0, Q1, Q2, Q3, Q4, Q5, Q6, Q7, Q8, Q9]), "depth" : 1.5 * mm});
        }
        {
            var Q0;
            {var subQ0=sQuery(id+"F0.wireOp",EDGE,"E47");var subQ1=makeQuery(id+"F0.imprint","INTERSECT",VERTEX,{"derivedFrom":[sQuery(id+"F0.wireOp",EDGE,"E45.top"),subQ0]});Q0=makeQuery(id+"F0.imprint","IMPRINT",FACE,{"disambiguationData":[TD([[makeQuery(id+"F0.imprint","IMPRINT",EDGE,{"disambiguationData":[TD([[subQ1,1.0]])],"derivedFrom":subQ0}),1.0]])]});}
            var Q1;
            {var subQ0=sQuery(id+"F0.wireOp",EDGE,"E48");var subQ1=makeQuery(id+"F0.imprint","INTERSECT",VERTEX,{"derivedFrom":[sQuery(id+"F0.wireOp",EDGE,"E46.top"),subQ0]});Q1=makeQuery(id+"F0.imprint","IMPRINT",FACE,{"disambiguationData":[TD([[makeQuery(id+"F0.imprint","IMPRINT",EDGE,{"disambiguationData":[TD([[subQ1,-1.0]])],"derivedFrom":subQ0}),1.0]])]});}
            extrude(context, id + "F9", {"entities" : qUnion([Q0, Q1]), "depth" : 7.5 * mm});
        }
        {
            var Q0;
            Q0=makeQuery(id+"F0.imprint","IMPRINT",FACE,{"disambiguationData":[TD([[makeQuery(id+"F0.imprint","IMPRINT",EDGE,{"derivedFrom":sQuery(id+"F0.wireOp",EDGE,"E49.bottom")}),-1.0]])]});
            extrude(context, id + "F10", {"entities" : qUnion([Q0]), "depth" : 5 * mm});
        }
        {
            var Q0;
            Q0=makeQuery(id+"F0.imprint","IMPRINT",FACE,{"disambiguationData":[TD([[makeQuery(id+"F0.imprint","IMPRINT",EDGE,{"derivedFrom":sQuery(id+"F0.wireOp",EDGE,"E50.bottom")}),-1.0]])]});
            var Q1;
            Q1=makeQuery(id+"F0.imprint","IMPRINT",FACE,{"disambiguationData":[TD([[makeQuery(id+"F0.imprint","IMPRINT",EDGE,{"derivedFrom":sQuery(id+"F0.wireOp",EDGE,"E51")}),1.0]])]});
            extrude(context, id + "F11", {"entities" : qUnion([Q0, Q1]), "depth" : 2 * mm});
        }
        {
            var Q0;
            Q0=makeQuery(id+"F0.imprint","IMPRINT",FACE,{"disambiguationData":[TD([[makeQuery(id+"F0.imprint","IMPRINT",EDGE,{"derivedFrom":sQuery(id+"F0.wireOp",EDGE,"E51")}),1.0]])]});
            extrude(context, id + "F12", {"entities" : qUnion([Q0]), "depth" : 3 * mm});
        }
        {
            var Q0;
            Q0=makeQuery(id+"F0.imprint","IMPRINT",FACE,{"disambiguationData":[TD([[makeQuery(id+"F0.imprint","IMPRINT",EDGE,{"derivedFrom":sQuery(id+"F0.wireOp",EDGE,"E59")}),1.0]])]});
            var Q1;
            Q1=makeQuery(id+"F0.imprint","IMPRINT",FACE,{"disambiguationData":[TD([[makeQuery(id+"F0.imprint","IMPRINT",EDGE,{"derivedFrom":sQuery(id+"F0.wireOp",EDGE,"E62")}),1.0]])]});
            var Q2;
            Q2=makeQuery(id+"F0.imprint","IMPRINT",FACE,{"disambiguationData":[TD([[makeQuery(id+"F0.imprint","IMPRINT",EDGE,{"derivedFrom":sQuery(id+"F0.wireOp",EDGE,"E65")}),1.0]])]});
            var Q3;
            Q3=makeQuery(id+"F0.imprint","IMPRINT",FACE,{"disambiguationData":[TD([[makeQuery(id+"F0.imprint","IMPRINT",EDGE,{"derivedFrom":sQuery(id+"F0.wireOp",EDGE,"E68")}),-1.0]])]});
            extrude(context, id + "F13", {"entities" : qUnion([Q0, Q1, Q2, Q3]), "operationType" : NewBodyOperationType.ADD, "depth" : 2.25 * mm});
        }
        {
            var Q0;
            Q0=makeQuery(id+"F2.opExtrude","SWEPT_FACE",FACE,{"disambiguationData":[OSD([sQuery(id+"F0.wireOp",EDGE,"E0.right"),sQuery(id+"F0.wireOp",EDGE,"E27.left")])]});
            var sketch = newSketch(context, id + "F14", { "sketchPlane" : qUnion([Q0])});
            skLineSegment(sketch, "E72.bottom", {"start": v(12.58, 0) * mm, "end": v(21.58, 0) * mm});
            skLineSegment(sketch, "E72.top", {"start": v(12.58, -1) * mm, "end": v(21.58, -1) * mm});
            skLineSegment(sketch, "E72.left", {"start": v(12.58, 0) * mm, "end": v(12.58, -1) * mm});
            skLineSegment(sketch, "E72.right", {"start": v(21.58, 0) * mm, "end": v(21.58, -1) * mm});
            skPoint(sketch, "E73.oppositeSnap0", {"position": v(21.58, -0.5) * mm});
            skLineSegment(sketch, "E73.top", {"start": v(12.58, 0.5) * mm, "end": v(21.58, 0.5) * mm});
            skLineSegment(sketch, "E73.left", {"start": v(12.58, 0) * mm, "end": v(12.58, 0.5) * mm});
            skLineSegment(sketch, "E73.right", {"start": v(21.58, 0) * mm, "end": v(21.58, 0.5) * mm});
            skLineSegment(sketch, "E74.top", {"start": v(12.58, 9) * mm, "end": v(21.58, 9) * mm});
            skLineSegment(sketch, "E74.left", {"start": v(12.58, 0) * mm, "end": v(12.58, 9) * mm});
            skLineSegment(sketch, "E74.right", {"start": v(21.58, 0) * mm, "end": v(21.58, 9) * mm});
            skCircle(sketch, "E75", {"center": v(17.08, 4.5) * mm, "radius": 3.75 * mm});
            skPoint(sketch, "E75.centerSnap0", {"position": v(21.58, 4.5) * mm});
            skPoint(sketch, "E75.centerSnap1", {"position": v(17.08, 9) * mm});
            skCircle(sketch, "E76", {"center": v(17.08, 4.5) * mm, "radius": 0.5 * mm});
            skCircle(sketch, "E77", {"center": v(17.08, 4.5) * mm, "radius": 3.5 * mm});
            skLineSegment(sketch, "E78", {"start": v(12.58, 4.5) * mm, "end": v(21.58, 4.5) * mm});
            skLineSegment(sketch, "E79.bottom", {"start": v(-17.15, 0) * mm, "end": v(-9.15, 0) * mm});
            skLineSegment(sketch, "E79.top", {"start": v(-17.15, 3) * mm, "end": v(-9.15, 3) * mm});
            skLineSegment(sketch, "E79.left", {"start": v(-17.15, 0) * mm, "end": v(-17.15, 3) * mm});
            skLineSegment(sketch, "E79.right", {"start": v(-9.15, 0) * mm, "end": v(-9.15, 3) * mm});
            skLineSegment(sketch, "E80.bottom", {"start": v(-16.9, 2.75) * mm, "end": v(-9.4, 2.75) * mm});
            skLineSegment(sketch, "E80.top", {"start": v(-16.9, 0.25) * mm, "end": v(-9.4, 0.25) * mm});
            skLineSegment(sketch, "E80.left", {"start": v(-16.9, 2.75) * mm, "end": v(-16.9, 0.25) * mm});
            skLineSegment(sketch, "E80.right", {"start": v(-9.4, 2.75) * mm, "end": v(-9.4, 0.25) * mm});
            skPoint(sketch, "E80.middle", {"position": v(-13.15, 1.5) * mm});
            skPoint(sketch, "E80.middle.positionSnap0", {"position": v(-9.15, 1.5) * mm});
            skPoint(sketch, "E80.middle.positionSnap1", {"position": v(-13.15, 3) * mm});
            skPoint(sketch, "E80.centerSnap0", {"position": v(-9.15, 1.5) * mm});
            skPoint(sketch, "E80.centerSnap1", {"position": v(-13.15, 3) * mm});
            skSolve(sketch);
        }
        {
            var Q0;
            {var subQ0=sQuery(id+"F14.wireOp",EDGE,"E73.top");Q0=makeQuery(id+"F14.imprint","IMPRINT",FACE,{"disambiguationData":[TD([[makeQuery(id+"F14.imprint","IMPRINT",EDGE,{"derivedFrom":subQ0}),-1.0]])]});}
            extrude(context, id + "F15", {"entities" : qUnion([Q0]), "oppositeDirection" : true, "depth" : 12 * mm});
        }
        {
            var Q0;
            Q0=makeQuery(id+"F15.opExtrude","CAP_FACE",FACE,{"disambiguationData":[OSD([sQuery(id+"F14.wireOp",EDGE,"E73.top"),sQuery(id+"F14.wireOp",EDGE,"E72.bottom"),sQuery(id+"F14.wireOp",EDGE,"E74.left"),sQuery(id+"F14.wireOp",EDGE,"E74.right")])],"isStart":true});
            extrude(context, id + "F16", {"entities" : qUnion([Q0]), "operationType" : NewBodyOperationType.ADD, "depth" : 3 * mm});
        }
        {
            var Q0;
            {var subQ5=sQuery(id+"F14.wireOp",EDGE,"E74.top");Q0=makeQuery(id+"F14.imprint","IMPRINT",FACE,{"disambiguationData":[TD([[makeQuery(id+"F14.imprint","IMPRINT",EDGE,{"derivedFrom":subQ5}),-1.0]])]});}
            var Q1;
            {var subQ1=sQuery(id+"F14.wireOp",EDGE,"E73.top");Q1=makeQuery(id+"F14.imprint","IMPRINT",FACE,{"disambiguationData":[TD([[makeQuery(id+"F14.imprint","IMPRINT",EDGE,{"derivedFrom":subQ1}),1.0]])]});}
            extrude(context, id + "F17", {"entities" : qUnion([Q0, Q1]), "operationType" : NewBodyOperationType.ADD, "endBound" : BoundingType.SYMMETRIC, "oppositeDirection" : true, "depth" : 6 * mm});
        }
        {
            var Q0;
            {var subQ1=sQuery(id+"F14.wireOp",EDGE,"E73.top");Q0=makeQuery(id+"F14.imprint","IMPRINT",FACE,{"disambiguationData":[TD([[makeQuery(id+"F14.imprint","IMPRINT",EDGE,{"derivedFrom":subQ1}),1.0]])]});}
            extrude(context, id + "F18", {"entities" : qUnion([Q0]), "operationType" : NewBodyOperationType.ADD, "oppositeDirection" : true, "depth" : 12 * mm});
        }
        {
            var Q0;
            {var subQ0=sQuery(id+"F14.wireOp",EDGE,"E78");var subQ1=sQuery(id+"F14.wireOp",EDGE,"E75");var subQ2=makeQuery(id+"F14.imprint","INTERSECT",VERTEX,{"disambiguationData":[OD(0.0)],"derivedFrom":[subQ1,subQ0]});Q0=makeQuery(id+"F14.imprint","IMPRINT",FACE,{"disambiguationData":[TD([[makeQuery(id+"F14.imprint","IMPRINT",EDGE,{"disambiguationData":[TD([[subQ2,1.0]])],"derivedFrom":subQ1}),1.0]])]});}
            var Q1;
            {var subQ0=sQuery(id+"F14.wireOp",EDGE,"E78");var subQ1=sQuery(id+"F14.wireOp",EDGE,"E75");var subQ2=makeQuery(id+"F14.imprint","INTERSECT",VERTEX,{"disambiguationData":[OD(0.0)],"derivedFrom":[subQ1,subQ0]});Q1=makeQuery(id+"F14.imprint","IMPRINT",FACE,{"disambiguationData":[TD([[makeQuery(id+"F14.imprint","IMPRINT",EDGE,{"disambiguationData":[TD([[subQ2,-1.0]])],"derivedFrom":subQ1}),1.0]])]});}
            var Q2;
            {var subQ0=sQuery(id+"F14.wireOp",EDGE,"E78");var subQ1=sQuery(id+"F14.wireOp",EDGE,"E76");var subQ2=makeQuery(id+"F14.imprint","INTERSECT",VERTEX,{"disambiguationData":[OD(0.0)],"derivedFrom":[subQ1,subQ0]});Q2=makeQuery(id+"F14.imprint","IMPRINT",FACE,{"disambiguationData":[TD([[makeQuery(id+"F14.imprint","IMPRINT",EDGE,{"disambiguationData":[TD([[subQ2,1.0]])],"derivedFrom":subQ1}),-1.0]])]});}
            var Q3;
            {var subQ0=sQuery(id+"F14.wireOp",EDGE,"E78");var subQ1=sQuery(id+"F14.wireOp",EDGE,"E76");var subQ2=makeQuery(id+"F14.imprint","INTERSECT",VERTEX,{"disambiguationData":[OD(0.0)],"derivedFrom":[subQ1,subQ0]});Q3=makeQuery(id+"F14.imprint","IMPRINT",FACE,{"disambiguationData":[TD([[makeQuery(id+"F14.imprint","IMPRINT",EDGE,{"disambiguationData":[TD([[subQ2,-1.0]])],"derivedFrom":subQ1}),-1.0]])]});}
            var Q4;
            {var subQ0=sQuery(id+"F14.wireOp",EDGE,"E78");var subQ1=sQuery(id+"F14.wireOp",EDGE,"E76");var subQ2=makeQuery(id+"F14.imprint","INTERSECT",VERTEX,{"disambiguationData":[OD(0.0)],"derivedFrom":[subQ1,subQ0]});Q4=makeQuery(id+"F14.imprint","IMPRINT",FACE,{"disambiguationData":[TD([[makeQuery(id+"F14.imprint","IMPRINT",EDGE,{"disambiguationData":[TD([[subQ2,1.0]])],"derivedFrom":subQ1}),1.0]])]});}
            var Q5;
            {var subQ0=sQuery(id+"F14.wireOp",EDGE,"E78");var subQ1=sQuery(id+"F14.wireOp",EDGE,"E76");var subQ2=makeQuery(id+"F14.imprint","INTERSECT",VERTEX,{"disambiguationData":[OD(0.0)],"derivedFrom":[subQ1,subQ0]});Q5=makeQuery(id+"F14.imprint","IMPRINT",FACE,{"disambiguationData":[TD([[makeQuery(id+"F14.imprint","IMPRINT",EDGE,{"disambiguationData":[TD([[subQ2,-1.0]])],"derivedFrom":subQ1}),1.0]])]});}
            extrude(context, id + "F19", {"entities" : qUnion([Q0, Q1, Q2, Q3, Q4, Q5]), "operationType" : NewBodyOperationType.ADD, "oppositeDirection" : true, "depth" : 12 * mm, "hasSecondDirection" : true, "secondDirectionOppositeDirection" : false, "secondDirectionDepth" : 3 * mm});
        }
        {
            var Q0;
            {var subQ0=sQuery(id+"F14.wireOp",EDGE,"E78");var subQ1=sQuery(id+"F14.wireOp",EDGE,"E76");var subQ2=makeQuery(id+"F14.imprint","INTERSECT",VERTEX,{"disambiguationData":[OD(0.0)],"derivedFrom":[subQ1,subQ0]});Q0=makeQuery(id+"F14.imprint","IMPRINT",FACE,{"disambiguationData":[TD([[makeQuery(id+"F14.imprint","IMPRINT",EDGE,{"disambiguationData":[TD([[subQ2,1.0]])],"derivedFrom":subQ1}),-1.0]])]});}
            var Q1;
            {var subQ0=sQuery(id+"F14.wireOp",EDGE,"E78");var subQ1=sQuery(id+"F14.wireOp",EDGE,"E76");var subQ2=makeQuery(id+"F14.imprint","INTERSECT",VERTEX,{"disambiguationData":[OD(0.0)],"derivedFrom":[subQ1,subQ0]});Q1=makeQuery(id+"F14.imprint","IMPRINT",FACE,{"disambiguationData":[TD([[makeQuery(id+"F14.imprint","IMPRINT",EDGE,{"disambiguationData":[TD([[subQ2,-1.0]])],"derivedFrom":subQ1}),-1.0]])]});}
            var Q2;
            {var subQ0=sQuery(id+"F14.wireOp",EDGE,"E78");var subQ1=sQuery(id+"F14.wireOp",EDGE,"E76");var subQ2=makeQuery(id+"F14.imprint","INTERSECT",VERTEX,{"disambiguationData":[OD(0.0)],"derivedFrom":[subQ1,subQ0]});Q2=makeQuery(id+"F14.imprint","IMPRINT",FACE,{"disambiguationData":[TD([[makeQuery(id+"F14.imprint","IMPRINT",EDGE,{"disambiguationData":[TD([[subQ2,-1.0]])],"derivedFrom":subQ1}),1.0]])]});}
            var Q3;
            {var subQ0=sQuery(id+"F14.wireOp",EDGE,"E78");var subQ1=sQuery(id+"F14.wireOp",EDGE,"E76");var subQ2=makeQuery(id+"F14.imprint","INTERSECT",VERTEX,{"disambiguationData":[OD(0.0)],"derivedFrom":[subQ1,subQ0]});Q3=makeQuery(id+"F14.imprint","IMPRINT",FACE,{"disambiguationData":[TD([[makeQuery(id+"F14.imprint","IMPRINT",EDGE,{"disambiguationData":[TD([[subQ2,1.0]])],"derivedFrom":subQ1}),1.0]])]});}
            extrude(context, id + "F20", {"entities" : qUnion([Q0, Q1, Q2, Q3]), "operationType" : NewBodyOperationType.REMOVE, "oppositeDirection" : true, "depth" : 11 * mm, "hasSecondDirection" : true, "secondDirectionOppositeDirection" : false, "secondDirectionDepth" : 3 * mm});
        }
        {
            var Q0;
            {var subQ0=sQuery(id+"F14.wireOp",EDGE,"E78");var subQ1=sQuery(id+"F14.wireOp",EDGE,"E76");var subQ2=makeQuery(id+"F14.imprint","INTERSECT",VERTEX,{"disambiguationData":[OD(0.0)],"derivedFrom":[subQ1,subQ0]});Q0=makeQuery(id+"F14.imprint","IMPRINT",FACE,{"disambiguationData":[TD([[makeQuery(id+"F14.imprint","IMPRINT",EDGE,{"disambiguationData":[TD([[subQ2,1.0]])],"derivedFrom":subQ1}),1.0]])]});}
            var Q1;
            {var subQ0=sQuery(id+"F14.wireOp",EDGE,"E78");var subQ1=sQuery(id+"F14.wireOp",EDGE,"E76");var subQ2=makeQuery(id+"F14.imprint","INTERSECT",VERTEX,{"disambiguationData":[OD(0.0)],"derivedFrom":[subQ1,subQ0]});Q1=makeQuery(id+"F14.imprint","IMPRINT",FACE,{"disambiguationData":[TD([[makeQuery(id+"F14.imprint","IMPRINT",EDGE,{"disambiguationData":[TD([[subQ2,-1.0]])],"derivedFrom":subQ1}),1.0]])]});}
            extrude(context, id + "F21", {"entities" : qUnion([Q0, Q1]), "oppositeDirection" : true, "depth" : 11 * mm, "hasSecondDirection" : true, "secondDirectionOppositeDirection" : false, "secondDirectionDepth" : 2 * mm});
        }
        {
            var Q0;
            Q0=makeQuery(id+"F14.imprint","IMPRINT",FACE,{"disambiguationData":[TD([[makeQuery(id+"F14.imprint","IMPRINT",EDGE,{"derivedFrom":sQuery(id+"F14.wireOp",EDGE,"E79.bottom")}),1.0]])]});
            var Q1;
            Q1=makeQuery(id+"F14.imprint","IMPRINT",FACE,{"disambiguationData":[TD([[makeQuery(id+"F14.imprint","IMPRINT",EDGE,{"derivedFrom":sQuery(id+"F14.wireOp",EDGE,"E80.bottom")}),-1.0]])]});
            extrude(context, id + "F22", {"entities" : qUnion([Q0, Q1]), "oppositeDirection" : true, "depth" : 5 * mm, "hasSecondDirection" : true, "secondDirectionOppositeDirection" : false, "secondDirectionDepth" : 2 * mm});
        }
        {
            var Q0;
            Q0=makeQuery(id+"F22.opExtrude","SWEPT_EDGE",EDGE,{"disambiguationData":[OSD([sQuery(id+"F14.wireOp",EDGE,"E79.top"),sQuery(id+"F14.wireOp",EDGE,"E79.right")])]});
            var Q1;
            Q1=makeQuery(id+"F22.opExtrude","SWEPT_EDGE",EDGE,{"disambiguationData":[OSD([sQuery(id+"F14.wireOp",EDGE,"E79.top"),sQuery(id+"F14.wireOp",EDGE,"E79.left")])]});
            fillet(context, id + "F23", {"entities" : qUnion([Q0, Q1]), "radius" : .5 * mm, "tangentPropagation" : true, "allowEdgeOverflow" : false});
        }
        {
            var Q0;
            Q0=makeQuery(id+"F14.imprint","IMPRINT",FACE,{"disambiguationData":[TD([[makeQuery(id+"F14.imprint","IMPRINT",EDGE,{"derivedFrom":sQuery(id+"F14.wireOp",EDGE,"E80.bottom")}),-1.0]])]});
            extrude(context, id + "F24", {"entities" : qUnion([Q0]), "operationType" : NewBodyOperationType.REMOVE, "oppositeDirection" : true, "depth" : 4.5 * mm, "hasSecondDirection" : true, "secondDirectionBound" : SecondDirectionBoundingType.THROUGH_ALL, "secondDirectionOppositeDirection" : false, "secondDirectionDepth" : 25 * mm});
        }
        {
            var Q0;
            Q0=makeQuery(id+"F0.imprint","IMPRINT",FACE,{"disambiguationData":[TD([[makeQuery(id+"F0.imprint","IMPRINT",EDGE,{"derivedFrom":sQuery(id+"F0.wireOp",EDGE,"E70.bottom")}),-1.0]])]});
            extrude(context, id + "F25", {"entities" : qUnion([Q0]), "operationType" : NewBodyOperationType.ADD, "depth" : 8 * mm});
        }
    });